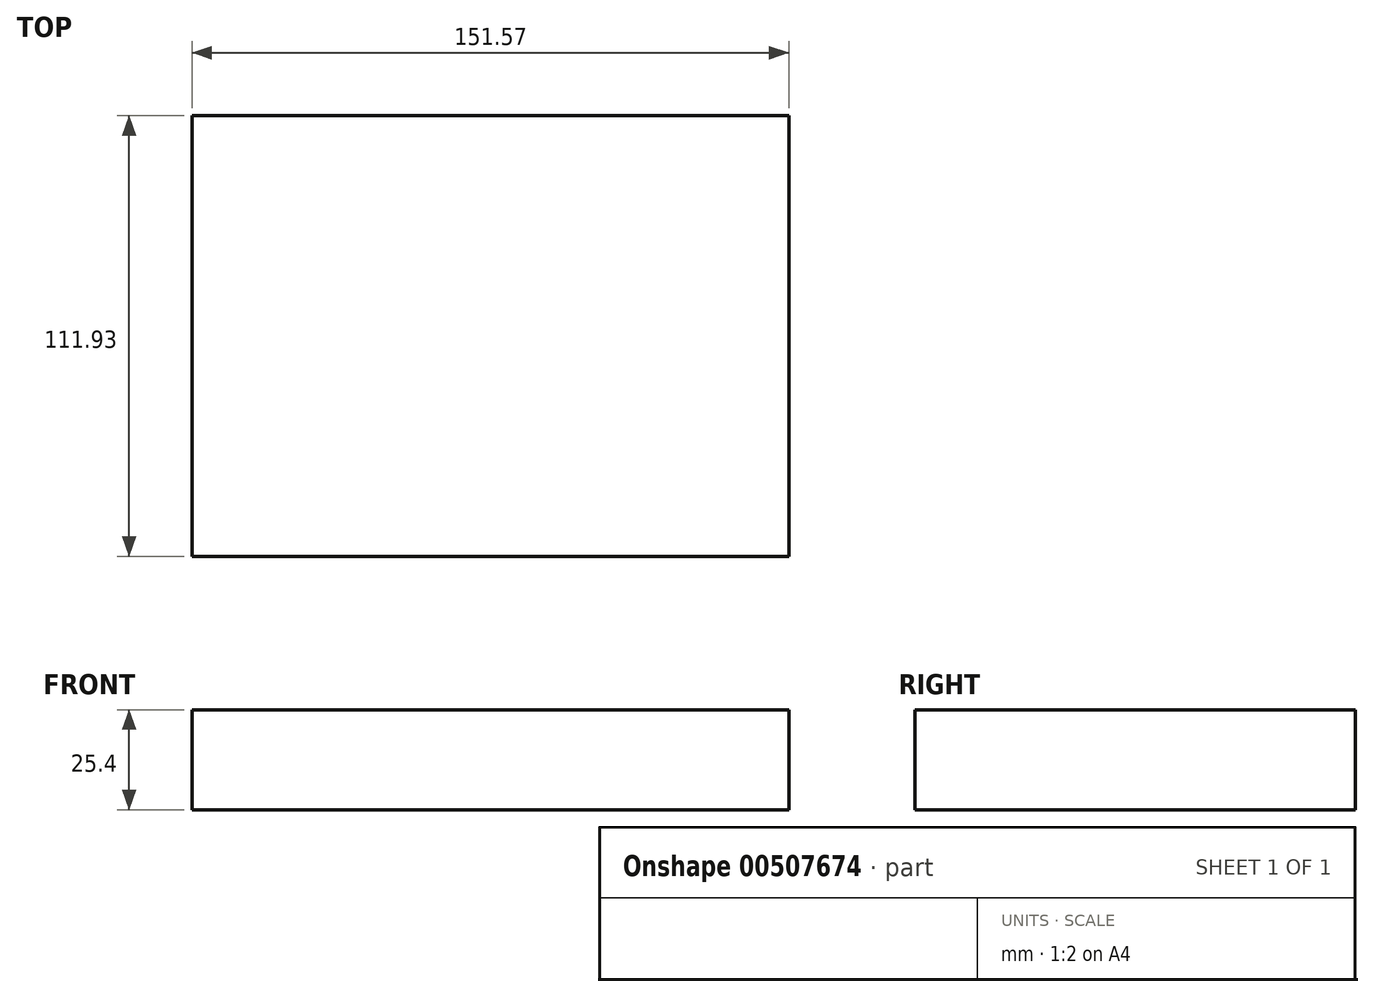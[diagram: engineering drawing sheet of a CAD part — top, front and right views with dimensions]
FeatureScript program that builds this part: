
annotation { "Feature Type Name" : "Feature", "Feature Type Description" : "" }
export const myFeature = defineFeature(function(context is Context, id is Id, definition is map)
    precondition{}
    {
        {
            var Q0;
            Q0=qCreatedBy(makeId("Top.planeOp"),FACE);
            var sketch = newSketch(context, id + "F0", { "sketchPlane" : qUnion([Q0])});
            skLineSegment(sketch, "E0.bottom", {"start": v(-76.08, -56.4) * mm, "end": v(75.5, -56.4) * mm});
            skLineSegment(sketch, "E0.top", {"start": v(-76.08, 55.53) * mm, "end": v(75.5, 55.53) * mm});
            skLineSegment(sketch, "E0.left", {"start": v(-76.08, -56.4) * mm, "end": v(-76.08, 55.53) * mm});
            skLineSegment(sketch, "E0.right", {"start": v(75.5, -56.4) * mm, "end": v(75.5, 55.53) * mm});
            skSolve(sketch);
        }
        {
            var Q0;
            Q0 = qSketchRegion(id + "F0", true);
            extrude(context, id + "F1", {"entities" : qUnion([Q0]), "depth" : 25.4 * mm});
        }
    });
